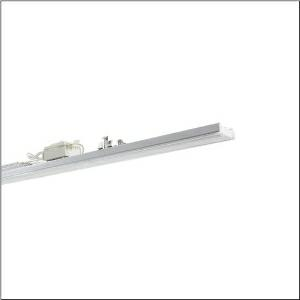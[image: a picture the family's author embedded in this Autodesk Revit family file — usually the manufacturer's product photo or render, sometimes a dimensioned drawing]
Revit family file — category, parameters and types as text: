
# Revit family: licross_r__21_recessed_ho_52te1emn4e5s_f825
name_source: partatom
category: Lighting Fixtures
units: mm (PartAtom-declared; Revit-internal decimal feet)

## family parameters
Cut with Voids When Loaded = No
Host = Face
Light Source = No
Part Type = Normal
Room Calculation Point = No
Round Connector Dimension = Use Diameter
Shared = No

## types (1)
- --- (1 x LED, 14710 lm, 83.1 W, 4000K)
    Apparent Load = 83 VA
    CIE Flux Codes = 85 95 99 100 100
    Color Rendering = 80
    Color Temperature = 4000K
    Default Elevation = 1800 mm
    Description = Licross® 21 Recessed HO, luminaire insert, of sheet steel, galvanised, coil coated, white, length: 1.500mm, width: 66mm, height: 67mm, LED rated luminous flux: 14.710lm, light colour: 840, control gear: ON/OFF Multilumen, with plug, 3-pole, with phase selection, mains connection: 220..240V, AC, 50/60Hz, rated input power: 83W, halogen-free wiring, primary light control with lens, of plastic, primary optical cover: cover, of PMMA, light emission: direct distribution, primary light characteristic: symmetric, protection rating (complete): IP54, insulation class (complete): insulation class I (protective earthing), certification: CE, ENEC, VDE, UKCA, protection symbol: D if used in an environment with non-conductive dust loads with corresponding accessories, impact resistance: IK06, permissible ambient temperature for indoor applications: -35..+30°C, corresponds to IFS (International Featured Standards) requirements for safety and quality in the food industry, reducing of maximum allowable ambient temperature of 5°C with ceiling mounting, LABS conformity tested according to VDMA 24364:2018-05, packaging unit: 1 piece
    Height = 58 mm
    Lamp = 1 x LED
    Lamp Light Flux = 14710 lm
    Lamp Power = 83.1 W
    Lamp count = 1
    Length = 1500 mm
    Luminous efficacy = 177 lm/W
    Manufacturer = Siteco
    ModVariant = No
    Model = 52TE1EMN4E5S
    Mounting Place = Ceiling
    Mounting Type = Pendant
    Number of Poles = 1
    OnlyDefault = Yes
    Power Factor = 1
    Product Name = Licross® 21 Recessed HO
    Product group = luminaire insert
    ProductGroupID = 902
    Protection Class = Protection class I
    Protection Degree = IP 54
    RLX_Detail_Level = 1
    RLX_Emergency_Light_Flux = 0 lm
    RLX_Emergency_Type = 0
    RLX_Emergency_Type_DB = No
    RlxData = <blob elided: 22333 chars, md5=60755864>
    Socket = socket
    Standby Power = 0 W
    System Light Flux = 14710 lm
    System Power = 83 W
    Type Comments = factory setting: luminous flux: 100 % | (A | C | E) | 195 mA
    Type Image = l_1296930.jpg
    URL = http://relux.com
    VarID = @adj_106478
    Voltage = 0 V
    Weight = 0.00 kg
    Width = 66 mm

## geometry (parser evidence)
native form markers: Blend x4, Sweep x10
no freeform markers — native parametric forms only
